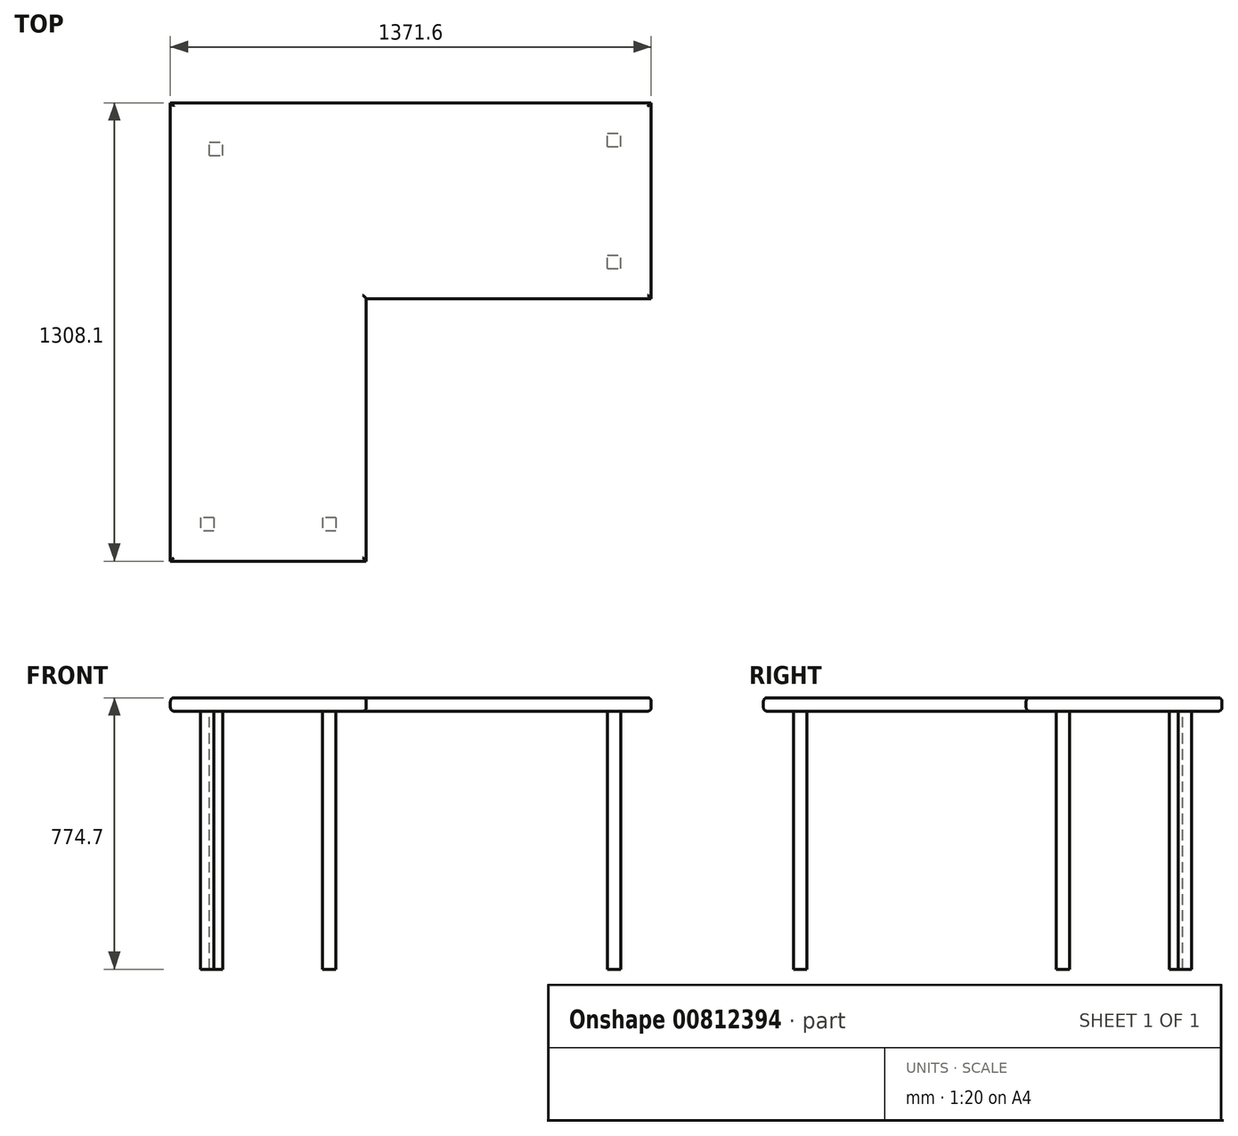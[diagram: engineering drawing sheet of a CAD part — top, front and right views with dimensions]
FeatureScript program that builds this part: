
annotation { "Feature Type Name" : "Feature", "Feature Type Description" : "" }
export const myFeature = defineFeature(function(context is Context, id is Id, definition is map)
    precondition{}
    {
        {
            var Q0;
            Q0=qCreatedBy(makeId("Top.planeOp"),FACE);
            var sketch = newSketch(context, id + "F0", { "sketchPlane" : qUnion([Q0])});
            skLineSegment(sketch, "E0", {"start": v(0, 0) * mm, "end": v(1371.6, 0) * mm});
            skLineSegment(sketch, "E1", {"start": v(1371.6, 0) * mm, "end": v(1371.6, -558.8) * mm});
            skLineSegment(sketch, "E2", {"start": v(1371.6, -558.8) * mm, "end": v(558.8, -558.8) * mm});
            skLineSegment(sketch, "E3", {"start": v(558.8, -558.8) * mm, "end": v(558.8, -1308.1) * mm});
            skLineSegment(sketch, "E4", {"start": v(558.8, -1308.1) * mm, "end": v(0, -1308.1) * mm});
            skLineSegment(sketch, "E5", {"start": v(0, 0) * mm, "end": v(0, -1308.1) * mm});
            skSolve(sketch);
        }
        {
            var Q0;
            Q0 = qSketchRegion(id + "F0", true);
            extrude(context, id + "F1", {"entities" : qUnion([Q0]), "depth" : 38.1 * mm, "offsetDistance" : 25.4 * mm});
        }
        {
            var Q0;
            Q0=makeQuery(id+"F1.opExtrude","CAP_EDGE",EDGE,{"disambiguationData":[OSD([sQuery(id+"F0.wireOp",EDGE,"E5")])],"isStart":false});
            var Q1;
            Q1=makeQuery(id+"F1.opExtrude","CAP_EDGE",EDGE,{"disambiguationData":[OSD([sQuery(id+"F0.wireOp",EDGE,"E4")])],"isStart":false});
            var Q2;
            Q2=makeQuery(id+"F1.opExtrude","CAP_EDGE",EDGE,{"disambiguationData":[OSD([sQuery(id+"F0.wireOp",EDGE,"E3")])],"isStart":false});
            var Q3;
            Q3=makeQuery(id+"F1.opExtrude","CAP_EDGE",EDGE,{"disambiguationData":[OSD([sQuery(id+"F0.wireOp",EDGE,"E2")])],"isStart":false});
            var Q4;
            Q4=makeQuery(id+"F1.opExtrude","CAP_EDGE",EDGE,{"disambiguationData":[OSD([sQuery(id+"F0.wireOp",EDGE,"E1")])],"isStart":false});
            var Q5;
            Q5=makeQuery(id+"F1.opExtrude","CAP_EDGE",EDGE,{"disambiguationData":[OSD([sQuery(id+"F0.wireOp",EDGE,"E0")])],"isStart":false});
            var Q6;
            Q6=makeQuery(id+"F1.opExtrude","CAP_EDGE",EDGE,{"disambiguationData":[OSD([sQuery(id+"F0.wireOp",EDGE,"E4")])],"isStart":true});
            var Q7;
            Q7=makeQuery(id+"F1.opExtrude","CAP_EDGE",EDGE,{"disambiguationData":[OSD([sQuery(id+"F0.wireOp",EDGE,"E5")])],"isStart":true});
            var Q8;
            Q8=makeQuery(id+"F1.opExtrude","CAP_EDGE",EDGE,{"disambiguationData":[OSD([sQuery(id+"F0.wireOp",EDGE,"E0")])],"isStart":true});
            var Q9;
            Q9=makeQuery(id+"F1.opExtrude","CAP_EDGE",EDGE,{"disambiguationData":[OSD([sQuery(id+"F0.wireOp",EDGE,"E1")])],"isStart":true});
            var Q10;
            Q10=makeQuery(id+"F1.opExtrude","CAP_EDGE",EDGE,{"disambiguationData":[OSD([sQuery(id+"F0.wireOp",EDGE,"E2")])],"isStart":true});
            var Q11;
            Q11=makeQuery(id+"F1.opExtrude","CAP_EDGE",EDGE,{"disambiguationData":[OSD([sQuery(id+"F0.wireOp",EDGE,"E3")])],"isStart":true});
            fillet(context, id + "F2", {"entities" : qUnion([Q0, Q1, Q2, Q3, Q4, Q5, Q6, Q7, Q8, Q9, Q10, Q11]), "radius" : 10.16 * mm, "tangentPropagation" : true, "allowEdgeOverflow" : false});
        }
        {
            var Q0;
            Q0=makeQuery(id+"F1.opExtrude","CAP_FACE",FACE,{"disambiguationData":[OSD([sQuery(id+"F0.wireOp",EDGE,"E0"),sQuery(id+"F0.wireOp",EDGE,"E1"),sQuery(id+"F0.wireOp",EDGE,"E2"),sQuery(id+"F0.wireOp",EDGE,"E3"),sQuery(id+"F0.wireOp",EDGE,"E4"),sQuery(id+"F0.wireOp",EDGE,"E5")])],"isStart":true});
            var sketch = newSketch(context, id + "F3", { "sketchPlane" : qUnion([Q0])});
            skLineSegment(sketch, "E6.bottom", {"start": v(111.76, 149.86) * mm, "end": v(149.86, 149.86) * mm});
            skLineSegment(sketch, "E6.top", {"start": v(111.76, 111.76) * mm, "end": v(149.86, 111.76) * mm});
            skLineSegment(sketch, "E6.left", {"start": v(111.76, 149.86) * mm, "end": v(111.76, 111.76) * mm});
            skLineSegment(sketch, "E6.right", {"start": v(149.86, 149.86) * mm, "end": v(149.86, 111.76) * mm});
            skPoint(sketch, "E6.middle", {"position": v(130.8, 130.8) * mm});
            skLineSegment(sketch, "E7.bottom", {"start": v(1247.14, 124.46) * mm, "end": v(1285.24, 124.46) * mm});
            skLineSegment(sketch, "E7.top", {"start": v(1247.14, 86.36) * mm, "end": v(1285.24, 86.36) * mm});
            skLineSegment(sketch, "E7.left", {"start": v(1247.14, 124.46) * mm, "end": v(1247.14, 86.36) * mm});
            skLineSegment(sketch, "E7.right", {"start": v(1285.24, 124.46) * mm, "end": v(1285.24, 86.36) * mm});
            skPoint(sketch, "E7.middle", {"position": v(1266.2, 105.4) * mm});
            skLineSegment(sketch, "E8.bottom", {"start": v(1247.14, 472.44) * mm, "end": v(1285.24, 472.44) * mm});
            skLineSegment(sketch, "E8.top", {"start": v(1247.14, 434.34) * mm, "end": v(1285.24, 434.34) * mm});
            skLineSegment(sketch, "E8.left", {"start": v(1247.14, 472.44) * mm, "end": v(1247.14, 434.34) * mm});
            skLineSegment(sketch, "E8.right", {"start": v(1285.24, 472.44) * mm, "end": v(1285.24, 434.34) * mm});
            skPoint(sketch, "E8.middle", {"position": v(1266.2, 453.4) * mm});
            skLineSegment(sketch, "E9.bottom", {"start": v(124.46, 1183.64) * mm, "end": v(86.36, 1183.64) * mm});
            skLineSegment(sketch, "E9.top", {"start": v(124.46, 1221.74) * mm, "end": v(86.36, 1221.74) * mm});
            skLineSegment(sketch, "E9.left", {"start": v(124.46, 1183.64) * mm, "end": v(124.46, 1221.74) * mm});
            skLineSegment(sketch, "E9.right", {"start": v(86.36, 1183.64) * mm, "end": v(86.36, 1221.74) * mm});
            skPoint(sketch, "E9.middle", {"position": v(105.4, 1202.7) * mm});
            skLineSegment(sketch, "E10.bottom", {"start": v(472.44, 1183.64) * mm, "end": v(434.34, 1183.64) * mm});
            skLineSegment(sketch, "E10.top", {"start": v(472.44, 1221.74) * mm, "end": v(434.34, 1221.74) * mm});
            skLineSegment(sketch, "E10.left", {"start": v(472.44, 1183.64) * mm, "end": v(472.44, 1221.74) * mm});
            skLineSegment(sketch, "E10.right", {"start": v(434.34, 1183.64) * mm, "end": v(434.34, 1221.74) * mm});
            skPoint(sketch, "E10.middle", {"position": v(453.4, 1202.7) * mm});
            skSolve(sketch);
        }
        {
            var Q0;
            Q0 = qSketchRegion(id + "F3", true);
            extrude(context, id + "F4", {"entities" : qUnion([Q0]), "operationType" : NewBodyOperationType.ADD, "depth" : 736.6 * mm, "offsetDistance" : 25.4 * mm});
        }
    });
